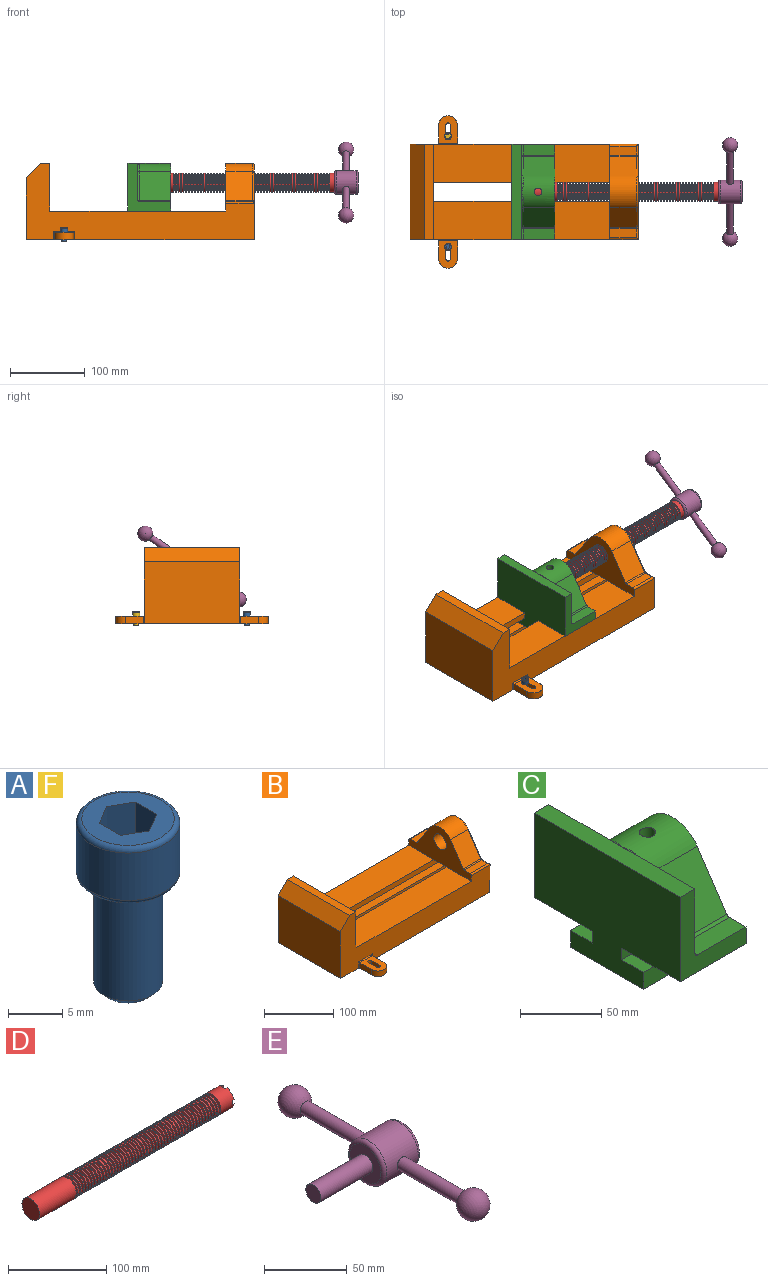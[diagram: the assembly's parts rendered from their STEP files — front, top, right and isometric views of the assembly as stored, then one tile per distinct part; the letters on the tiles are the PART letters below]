
ASSEMBLY  parts=6 mates=6
PART A: 15 faces, bbox 10.3x10.3x19.1 mm
  f0: plane 8.51x8.51mm, normal (0,0,1), area 37.2mm2, adj f5,f6,f7,f8,f9,f10,f14
  f1: cylinder r=3.17mm len=11.94mm, axis (0,0,1), area 238.2mm2, adj f4,f12
  f2: plane 4.83x4.83mm, normal (0,0,-1), area 18.3mm2, adj f12
  f3: cylinder r=4.76mm len=9.53mm, axis (0,0,-1), area 159.6mm2, adj f13,f14
  f4: plane 8.51x8.51mm, normal (0,0,-1), area 25.2mm2, adj f1,f13
  f5: plane 4.83x2.38mm, normal (-0.5,-0.87,0), area 13.3mm2, adj f0,f6,f10,f11
  f6: plane 4.83x2.38mm, normal (0.5,-0.87,0), area 13.3mm2, adj f0,f5,f7,f11
  f7: plane 4.83x2.75mm, normal (1,0,0), area 13.3mm2, adj f0,f6,f8,f11
  f8: plane 4.83x2.38mm, normal (0.5,0.87,0), area 13.3mm2, adj f0,f7,f9,f11
  f9: plane 4.83x2.38mm, normal (-0.5,0.87,0), area 13.3mm2, adj f0,f8,f10,f11
  f10: plane 4.83x2.75mm, normal (-1,0,0), area 13.3mm2, adj f0,f5,f9,f11
  f11: plane 5.5x4.76mm, normal (0,0,1), area 19.6mm2, adj f5,f6,f7,f8,f9,f10
  f12: cone r=3.17mm half-angle=45deg, axis (0,0,1), area 18.9mm2, adj f1,f2
  f13: torus R=4.25mm, axis (0,0,1), area 23mm2, adj f3,f4
  f14: torus R=4.25mm, axis (0,0,1), area 23mm2, adj f0,f3
PART B: 61 faces, bbox 304.8x203.2x103.7 mm
  f0: plane 304.8x101.6mm, normal (0,1,0), area 13520.3mm2, adj f3,f4,f5,f6,f7,f8,f9,f16
  f1: plane 304.8x101.6mm, normal (0,-1,0), area 13520.3mm2, adj f2,f3,f5,f6,f7,f8,f9,f16
  f2: plane 234.95x50.8mm, normal (0,0,1), area 11935.5mm2, adj f1,f5,f16,f26
  f3: plane 127x99.06mm, normal (1,0,0), area 7097.5mm2, adj f0,f1,f9,f14,f17,f18,f19,f20
  f4: plane 234.95x50.8mm, normal (0,0,1), area 11935.5mm2, adj f0,f5,f16,f27
  f5: plane 127x101.6mm, normal (1,0,0), area 9516.1mm2, adj f0,f1,f2,f4,f6,f9,f18,f19
  f6: plane 127x12.7mm, normal (0,0,1), area 1612.9mm2, adj f0,f1,f5,f7
  f7: plane 127x19.05mm, normal (-0.71,0,0.71), area 3421.5mm2, adj f0,f1,f6,f8
  f8: plane 127x82.55mm, normal (-1,0,0), area 10483.8mm2, adj f0,f1,f7,f9
  f9: plane 304.8x203.2mm, normal (0,0,-1), area 33298.3mm2, adj f0,f1,f3,f5,f8,f21,f22,f39
  f10: plane 35.56x11.98mm, normal (0,0,1), area 426mm2, adj f16,f28,f29,f30
  f11: plane 38.43x35.56mm, normal (0,0.83,0.56), area 1645.4mm2, adj f12,f16,f29,f32
  f12: cylinder r=25.4mm len=42.19mm, axis (1,0,0), area 1770.2mm2, adj f11,f13,f16,f33
  f13: plane 38.43x35.56mm, normal (0,-0.83,0.56), area 1645.4mm2, adj f12,f16,f34,f35
  f14: cylinder r=12.7mm len=38.1mm, axis (1,0,0), area 3040.2mm2, adj f3,f16
  f15: plane 35.56x11.98mm, normal (0,0,1), area 426mm2, adj f16,f34,f36,f38
  f16: plane 127x63.5mm, normal (-1,0,0), area 4155.5mm2, adj f0,f1,f2,f4,f10,f11,f12,f13
  f17: plane 38.1x25.4mm, normal (0,0,-1), area 967.7mm2, adj f3,f16,f26,f27
  f18: plane 273.05x19.05mm, normal (0,0,-1), area 5201.6mm2, adj f3,f5,f19,f26
  f19: plane 273.05x12.7mm, normal (0,1,0), area 3467.7mm2, adj f3,f5,f18,f20
  f20: plane 273.05x19.05mm, normal (0,0,1), area 5201.6mm2, adj f3,f5,f19,f21
  f21: plane 273.05x16.51mm, normal (0,1,0), area 4508.1mm2, adj f3,f5,f9,f20
  f22: plane 273.05x16.51mm, normal (0,-1,0), area 4508.1mm2, adj f3,f5,f9,f23
  f23: plane 273.05x19.05mm, normal (0,0,1), area 5201.6mm2, adj f3,f5,f22,f24
  f24: plane 273.05x12.7mm, normal (0,-1,0), area 3467.7mm2, adj f3,f5,f23,f25
  f25: plane 273.05x19.05mm, normal (0,0,-1), area 5201.6mm2, adj f3,f5,f24,f27
  f26: plane 273.05x8.89mm, normal (0,1,0), area 2427.4mm2, adj f2,f3,f5,f17,f18
  f27: plane 273.05x8.89mm, normal (0,-1,0), area 2427.4mm2, adj f3,f4,f5,f17,f25
  f28: cylinder r=2.54mm len=38.1mm, axis (1,0,0), area 148.3mm2, adj f0,f10,f16,f30
  f29: cylinder r=2.54mm len=35.56mm, axis (-1,0,0), area 88.5mm2, adj f10,f11,f16,f31
  f30: cylinder r=2.54mm len=14.52mm, axis (0,1,0), area 54.3mm2, adj f3,f10,f28,f31
  f31: torus R=5.08mm, axis (-1,0,0), area 13.5mm2, adj f3,f29,f30,f32
  f32: cylinder r=2.54mm len=39.84mm, axis (0,0.56,-0.83), area 184.6mm2, adj f3,f11,f31,f33
  f33: torus R=22.86mm, axis (-1,0,0), area 191.4mm2, adj f3,f12,f32,f35
  f34: cylinder r=2.54mm len=35.56mm, axis (-1,0,0), area 88.5mm2, adj f13,f15,f16,f37
  f35: cylinder r=2.54mm len=39.84mm, axis (0,0.56,0.83), area 184.6mm2, adj f3,f13,f33,f37
  f36: cylinder r=2.54mm len=38.1mm, axis (-1,0,0), area 148.3mm2, adj f1,f15,f16,f38
  f37: torus R=5.08mm, axis (-1,0,0), area 13.5mm2, adj f3,f34,f35,f38
  f38: cylinder r=2.54mm len=14.52mm, axis (0,1,0), area 54.3mm2, adj f3,f15,f36,f37
  f39: plane 23.88x9.53mm, normal (-1,0,0), area 227.4mm2, adj f9,f45,f46,f60
  f40: plane 23.88x9.53mm, normal (1,0,0), area 227.4mm2, adj f9,f45,f46,f58
  f41: cylinder r=3.3mm len=9.53mm, axis (0,0,-1), area 98.8mm2, adj f9,f42,f44,f46
  f42: plane 15.62x9.53mm, normal (-1,0,0), area 148.8mm2, adj f9,f41,f43,f46
  f43: cylinder r=3.3mm len=9.53mm, axis (0,0,-1), area 98.8mm2, adj f9,f42,f44,f46
  f44: plane 15.62x9.53mm, normal (1,0,0), area 148.8mm2, adj f9,f41,f43,f46
  f45: cylinder r=12.7mm len=25.4mm, axis (0,0,-1), area 380mm2, adj f9,f39,f40,f46
  f46: plane 36.58x25.4mm, normal (0,0,1), area 722.4mm2, adj f39,f40,f41,f42,f43,f44,f45,f59
  f47: plane 23.88x9.53mm, normal (-1,0,0), area 227.4mm2, adj f9,f53,f54,f56
  f48: plane 23.88x9.53mm, normal (1,0,0), area 227.4mm2, adj f9,f53,f54,f55
  f49: cylinder r=3.3mm len=9.53mm, axis (0,0,-1), area 98.8mm2, adj f9,f50,f52,f54
  f50: plane 15.62x9.53mm, normal (-1,0,0), area 148.8mm2, adj f9,f49,f51,f54
  f51: cylinder r=3.3mm len=9.53mm, axis (0,0,-1), area 98.8mm2, adj f9,f50,f52,f54
  f52: plane 15.62x9.53mm, normal (1,0,0), area 148.8mm2, adj f9,f49,f51,f54
  f53: cylinder r=12.7mm len=25.4mm, axis (0,0,-1), area 380mm2, adj f9,f47,f48,f54
  f54: plane 36.58x25.4mm, normal (0,0,1), area 722.4mm2, adj f47,f48,f49,f50,f51,f52,f53,f57
  f55: cylinder r=1.52mm len=11.05mm, axis (0,0,-1), area 24.1mm2, adj f0,f9,f48,f57
  f56: cylinder r=1.52mm len=11.05mm, axis (0,0,1), area 24.1mm2, adj f0,f9,f47,f57
  f57: cylinder r=1.52mm len=28.45mm, axis (1,0,0), area 63.5mm2, adj f0,f54,f55,f56
  f58: cylinder r=1.52mm len=11.05mm, axis (0,0,1), area 24.1mm2, adj f1,f9,f40,f59
  f59: cylinder r=1.52mm len=28.45mm, axis (-1,0,0), area 63.5mm2, adj f1,f46,f58,f60
  f60: cylinder r=1.52mm len=11.05mm, axis (0,0,-1), area 24.1mm2, adj f1,f9,f39,f59
PART C: 36 faces, bbox 57.2x127x89 mm
  f0: plane 57.15x50.8mm, normal (0,0,-1), area 2903.2mm2, adj f6,f9,f10,f23
  f1: cylinder r=12.7mm len=44.45mm, axis (1,0,0), area 3464.3mm2, adj f6,f15,f16
  f2: plane 41.91x14.52mm, normal (0,0,1), area 608.5mm2, adj f6,f11,f24,f25
  f3: plane 51.86x48.26mm, normal (1,0,0), area 1495.7mm2, adj f8,f10,f31,f33,f35
  f4: plane 51.86x48.26mm, normal (1,0,0), area 1495.7mm2, adj f8,f11,f24,f28,f29
  f5: plane 57.15x50.8mm, normal (0,0,-1), area 2903.2mm2, adj f6,f9,f11,f22
  f6: plane 127x85.09mm, normal (1,0,0), area 5190.6mm2, adj f0,f1,f2,f5,f7,f10,f11,f12
  f7: plane 41.91x14.52mm, normal (0,0,1), area 608.5mm2, adj f6,f10,f30,f31
  f8: plane 127x12.7mm, normal (0,0,1), area 1612.9mm2, adj f3,f4,f9,f10,f11,f26,f34
  f9: plane 127x85.09mm, normal (-1,0,0), area 9096.8mm2, adj f0,f5,f8,f10,f11,f17,f18,f19
  f10: plane 63.5x57.15mm, normal (0,-1,0), area 1372.3mm2, adj f0,f3,f6,f7,f8,f9,f31
  f11: plane 63.5x57.15mm, normal (0,1,0), area 1372.3mm2, adj f2,f4,f5,f6,f8,f9,f24
  f12: plane 41.91x38.43mm, normal (0,-0.83,0.56), area 1939.2mm2, adj f6,f13,f30,f33
  f13: cylinder r=25.4mm len=44.45mm, axis (1,0,0), area 2026.5mm2, adj f6,f12,f14,f16,f26,f28,f34,f35
  f14: plane 41.91x38.43mm, normal (0,0.83,0.56), area 1939.2mm2, adj f6,f13,f25,f29
  f15: plane 25.4x25.4mm, normal (1,0,0), area 506.7mm2, adj f1
  f16: cylinder r=5.08mm len=13.76mm, axis (0,0,1), area 414mm2, adj f1,f13
  f17: plane 57.15x19.05mm, normal (0,0,1), area 1088.7mm2, adj f6,f9,f18,f23
  f18: plane 57.15x12.7mm, normal (0,-1,0), area 725.8mm2, adj f6,f9,f17,f19
  f19: plane 63.5x57.15mm, normal (0,0,-1), area 3629mm2, adj f6,f9,f18,f20
  f20: plane 57.15x12.7mm, normal (0,1,0), area 725.8mm2, adj f6,f9,f19,f21
  f21: plane 57.15x19.05mm, normal (0,0,1), area 1088.7mm2, adj f6,f9,f20,f22
  f22: plane 57.15x8.89mm, normal (0,1,0), area 508.1mm2, adj f5,f6,f9,f21
  f23: plane 57.15x8.89mm, normal (0,-1,0), area 508.1mm2, adj f0,f6,f9,f17
  f24: cylinder r=2.54mm len=14.52mm, axis (0,-1,0), area 57.9mm2, adj f2,f4,f11,f27
  f25: cylinder r=2.54mm len=41.91mm, axis (1,0,0), area 104.3mm2, adj f2,f6,f14,f27
  f26: bspline ~12.24x2.8mm, area 20.9mm2, adj f8,f13,f28
  f27: sphere r=2.54mm, area 6.3mm2, adj f24,f25,f29
  f28: torus R=27.94mm, axis (1,0,0), area 57.8mm2, adj f4,f13,f26,f29
  f29: cylinder r=2.54mm len=39.84mm, axis (0,-0.56,0.83), area 184.6mm2, adj f4,f14,f27,f28
  f30: cylinder r=2.54mm len=41.91mm, axis (1,0,0), area 104.3mm2, adj f6,f7,f12,f32
  f31: cylinder r=2.54mm len=14.52mm, axis (0,-1,0), area 57.9mm2, adj f3,f7,f10,f32
  f32: sphere r=2.54mm, area 6.3mm2, adj f30,f31,f33
  f33: cylinder r=2.54mm len=39.84mm, axis (0,-0.56,-0.83), area 184.6mm2, adj f3,f12,f32,f35
  f34: bspline ~12.24x2.8mm, area 20.9mm2, adj f8,f13,f35
  f35: torus R=27.94mm, axis (1,0,0), area 57.8mm2, adj f3,f13,f33,f34
PART D: 220 faces, bbox 279.4x25.4x25.4 mm
  f0: cylinder r=12.7mm len=25.4mm, axis (-1,0,0), area 1468.2mm2, adj f1,f2,f3,f5,f7,f208,f209,f210
  f1: plane 9.9x9.9mm, normal (1,0,0), area 62.3mm2, adj f0,f4,f213,f216
  f2: plane 9.9x9.9mm, normal (1,0,0), area 62.3mm2, adj f0,f4,f210,f218
  f3: plane 9.9x9.9mm, normal (1,0,0), area 62.3mm2, adj f0,f4,f209,f212
  f4: cylinder r=6.35mm len=25.4mm, axis (1,0,0), area 960.3mm2, adj f1,f2,f3,f5,f6,f208,f209,f210
  f5: plane 9.9x9.9mm, normal (1,0,0), area 62.3mm2, adj f0,f4,f215,f217
  f6: plane 12.7x12.7mm, normal (1,0,0), area 126.7mm2, adj f4
  f7: cone r=12.7mm half-angle=76deg, axis (1,0,0), area 188mm2, adj f0,f9
  f8: cone r=10.16mm half-angle=76deg, axis (-1,0,0), area 188mm2, adj f9,f10
  f9: cylinder r=10.16mm len=20.32mm, axis (1,0,0), area 81.1mm2, adj f7,f8
  f10: cylinder r=12.7mm len=25.4mm, axis (-1,0,0), area 131.7mm2, adj f8,f11
  f11: cone r=12.7mm half-angle=76deg, axis (1,0,0), area 188mm2, adj f10,f13
  f12: cone r=10.16mm half-angle=76deg, axis (-1,0,0), area 188mm2, adj f13,f14
  f13: cylinder r=10.16mm len=20.32mm, axis (1,0,0), area 81.1mm2, adj f11,f12
  f14: cylinder r=12.7mm len=25.4mm, axis (-1,0,0), area 131.7mm2, adj f12,f15
  f15: cone r=12.7mm half-angle=76deg, axis (1,0,0), area 188mm2, adj f14,f17
  f16: cone r=10.16mm half-angle=76deg, axis (-1,0,0), area 188mm2, adj f17,f18
  f17: cylinder r=10.16mm len=20.32mm, axis (1,0,0), area 81.1mm2, adj f15,f16
  f18: cylinder r=12.7mm len=25.4mm, axis (-1,0,0), area 131.7mm2, adj f16,f19
  f19: cone r=12.7mm half-angle=76deg, axis (1,0,0), area 188mm2, adj f18,f21
  f20: cone r=10.16mm half-angle=76deg, axis (-1,0,0), area 188mm2, adj f21,f22
  f21: cylinder r=10.16mm len=20.32mm, axis (1,0,0), area 81.1mm2, adj f19,f20
  f22: cylinder r=12.7mm len=25.4mm, axis (-1,0,0), area 131.7mm2, adj f20,f23
  f23: cone r=12.7mm half-angle=76deg, axis (1,0,0), area 188mm2, adj f22,f25
  f24: cone r=10.16mm half-angle=76deg, axis (-1,0,0), area 188mm2, adj f25,f26
  f25: cylinder r=10.16mm len=20.32mm, axis (1,0,0), area 81.1mm2, adj f23,f24
  f26: cylinder r=12.7mm len=25.4mm, axis (-1,0,0), area 131.7mm2, adj f24,f27
  f27: cone r=12.7mm half-angle=76deg, axis (1,0,0), area 188mm2, adj f26,f29
  f28: cone r=10.16mm half-angle=76deg, axis (-1,0,0), area 188mm2, adj f29,f30
  f29: cylinder r=10.16mm len=20.32mm, axis (1,0,0), area 81.1mm2, adj f27,f28
  f30: cylinder r=12.7mm len=25.4mm, axis (-1,0,0), area 131.7mm2, adj f28,f31
  f31: cone r=12.7mm half-angle=76deg, axis (1,0,0), area 188mm2, adj f30,f33
  f32: cone r=10.16mm half-angle=76deg, axis (-1,0,0), area 188mm2, adj f33,f34
  f33: cylinder r=10.16mm len=20.32mm, axis (1,0,0), area 81.1mm2, adj f31,f32
  f34: cylinder r=12.7mm len=25.4mm, axis (-1,0,0), area 131.7mm2, adj f32,f35
  f35: cone r=12.7mm half-angle=76deg, axis (1,0,0), area 188mm2, adj f34,f37
  f36: cone r=10.16mm half-angle=76deg, axis (-1,0,0), area 188mm2, adj f37,f38
  f37: cylinder r=10.16mm len=20.32mm, axis (1,0,0), area 81.1mm2, adj f35,f36
  f38: cylinder r=12.7mm len=25.4mm, axis (-1,0,0), area 131.7mm2, adj f36,f39
  f39: cone r=12.7mm half-angle=76deg, axis (1,0,0), area 188mm2, adj f38,f41
  f40: cone r=10.16mm half-angle=76deg, axis (-1,0,0), area 188mm2, adj f41,f42
  f41: cylinder r=10.16mm len=20.32mm, axis (1,0,0), area 81.1mm2, adj f39,f40
  f42: cylinder r=12.7mm len=25.4mm, axis (-1,0,0), area 131.7mm2, adj f40,f43
  f43: cone r=12.7mm half-angle=76deg, axis (1,0,0), area 188mm2, adj f42,f45
  f44: cone r=10.16mm half-angle=76deg, axis (-1,0,0), area 188mm2, adj f45,f46
  f45: cylinder r=10.16mm len=20.32mm, axis (1,0,0), area 81.1mm2, adj f43,f44
  f46: cylinder r=12.7mm len=25.4mm, axis (-1,0,0), area 131.7mm2, adj f44,f47
  f47: cone r=12.7mm half-angle=76deg, axis (1,0,0), area 188mm2, adj f46,f49
  f48: cone r=10.16mm half-angle=76deg, axis (-1,0,0), area 188mm2, adj f49,f50
  f49: cylinder r=10.16mm len=20.32mm, axis (1,0,0), area 81.1mm2, adj f47,f48
  f50: cylinder r=12.7mm len=25.4mm, axis (-1,0,0), area 131.7mm2, adj f48,f51
  f51: cone r=12.7mm half-angle=76deg, axis (1,0,0), area 188mm2, adj f50,f53
  f52: cone r=10.16mm half-angle=76deg, axis (-1,0,0), area 188mm2, adj f53,f54
  f53: cylinder r=10.16mm len=20.32mm, axis (1,0,0), area 81.1mm2, adj f51,f52
  f54: cylinder r=12.7mm len=25.4mm, axis (-1,0,0), area 131.7mm2, adj f52,f55
  f55: cone r=12.7mm half-angle=76deg, axis (1,0,0), area 188mm2, adj f54,f57
  f56: cone r=10.16mm half-angle=76deg, axis (-1,0,0), area 188mm2, adj f57,f58
  f57: cylinder r=10.16mm len=20.32mm, axis (1,0,0), area 81.1mm2, adj f55,f56
  f58: cylinder r=12.7mm len=25.4mm, axis (-1,0,0), area 131.7mm2, adj f56,f59
  f59: cone r=12.7mm half-angle=76deg, axis (1,0,0), area 188mm2, adj f58,f61
  f60: cone r=10.16mm half-angle=76deg, axis (-1,0,0), area 188mm2, adj f61,f62
  f61: cylinder r=10.16mm len=20.32mm, axis (1,0,0), area 81.1mm2, adj f59,f60
  f62: cylinder r=12.7mm len=25.4mm, axis (-1,0,0), area 131.7mm2, adj f60,f63
  f63: cone r=12.7mm half-angle=76deg, axis (1,0,0), area 188mm2, adj f62,f65
  f64: cone r=10.16mm half-angle=76deg, axis (-1,0,0), area 188mm2, adj f65,f66
  f65: cylinder r=10.16mm len=20.32mm, axis (1,0,0), area 81.1mm2, adj f63,f64
  f66: cylinder r=12.7mm len=25.4mm, axis (-1,0,0), area 131.7mm2, adj f64,f67
  f67: cone r=12.7mm half-angle=76deg, axis (1,0,0), area 188mm2, adj f66,f69
  f68: cone r=10.16mm half-angle=76deg, axis (-1,0,0), area 188mm2, adj f69,f70
  f69: cylinder r=10.16mm len=20.32mm, axis (1,0,0), area 81.1mm2, adj f67,f68
  f70: cylinder r=12.7mm len=25.4mm, axis (-1,0,0), area 131.7mm2, adj f68,f71
  f71: cone r=12.7mm half-angle=76deg, axis (1,0,0), area 188mm2, adj f70,f73
  f72: cone r=10.16mm half-angle=76deg, axis (-1,0,0), area 188mm2, adj f73,f74
  f73: cylinder r=10.16mm len=20.32mm, axis (1,0,0), area 81.1mm2, adj f71,f72
  f74: cylinder r=12.7mm len=25.4mm, axis (-1,0,0), area 131.7mm2, adj f72,f75
  f75: cone r=12.7mm half-angle=76deg, axis (1,0,0), area 188mm2, adj f74,f77
  f76: cone r=10.16mm half-angle=76deg, axis (-1,0,0), area 188mm2, adj f77,f78
  f77: cylinder r=10.16mm len=20.32mm, axis (1,0,0), area 81.1mm2, adj f75,f76
  f78: cylinder r=12.7mm len=25.4mm, axis (-1,0,0), area 131.7mm2, adj f76,f79
  f79: cone r=12.7mm half-angle=76deg, axis (1,0,0), area 188mm2, adj f78,f81
  f80: cone r=10.16mm half-angle=76deg, axis (-1,0,0), area 188mm2, adj f81,f82
  f81: cylinder r=10.16mm len=20.32mm, axis (1,0,0), area 81.1mm2, adj f79,f80
  f82: cylinder r=12.7mm len=25.4mm, axis (-1,0,0), area 131.7mm2, adj f80,f83
  f83: cone r=12.7mm half-angle=76deg, axis (1,0,0), area 188mm2, adj f82,f85
  f84: cone r=10.16mm half-angle=76deg, axis (-1,0,0), area 188mm2, adj f85,f86
  f85: cylinder r=10.16mm len=20.32mm, axis (1,0,0), area 81.1mm2, adj f83,f84
  f86: cylinder r=12.7mm len=25.4mm, axis (-1,0,0), area 131.7mm2, adj f84,f87
  f87: cone r=12.7mm half-angle=76deg, axis (1,0,0), area 188mm2, adj f86,f89
  f88: cone r=10.16mm half-angle=76deg, axis (-1,0,0), area 188mm2, adj f89,f90
  f89: cylinder r=10.16mm len=20.32mm, axis (1,0,0), area 81.1mm2, adj f87,f88
  f90: cylinder r=12.7mm len=25.4mm, axis (-1,0,0), area 131.7mm2, adj f88,f91
  f91: cone r=12.7mm half-angle=76deg, axis (1,0,0), area 188mm2, adj f90,f93
  f92: cone r=10.16mm half-angle=76deg, axis (-1,0,0), area 188mm2, adj f93,f94
  f93: cylinder r=10.16mm len=20.32mm, axis (1,0,0), area 81.1mm2, adj f91,f92
  f94: cylinder r=12.7mm len=25.4mm, axis (-1,0,0), area 131.7mm2, adj f92,f95
  f95: cone r=12.7mm half-angle=76deg, axis (1,0,0), area 188mm2, adj f94,f97
  f96: cone r=10.16mm half-angle=76deg, axis (-1,0,0), area 188mm2, adj f97,f98
  f97: cylinder r=10.16mm len=20.32mm, axis (1,0,0), area 81.1mm2, adj f95,f96
  f98: cylinder r=12.7mm len=25.4mm, axis (-1,0,0), area 131.7mm2, adj f96,f99
  f99: cone r=12.7mm half-angle=76deg, axis (1,0,0), area 188mm2, adj f98,f101
  f100: cone r=10.16mm half-angle=76deg, axis (-1,0,0), area 188mm2, adj f101,f102
  f101: cylinder r=10.16mm len=20.32mm, axis (1,0,0), area 81.1mm2, adj f99,f100
  f102: cylinder r=12.7mm len=25.4mm, axis (-1,0,0), area 131.7mm2, adj f100,f103
  f103: cone r=12.7mm half-angle=76deg, axis (1,0,0), area 188mm2, adj f102,f105
  f104: cone r=10.16mm half-angle=76deg, axis (-1,0,0), area 188mm2, adj f105,f106
  f105: cylinder r=10.16mm len=20.32mm, axis (1,0,0), area 81.1mm2, adj f103,f104
  f106: cylinder r=12.7mm len=25.4mm, axis (-1,0,0), area 131.7mm2, adj f104,f107
  f107: cone r=12.7mm half-angle=76deg, axis (1,0,0), area 188mm2, adj f106,f109
  f108: cone r=10.16mm half-angle=76deg, axis (-1,0,0), area 188mm2, adj f109,f110
  f109: cylinder r=10.16mm len=20.32mm, axis (1,0,0), area 81.1mm2, adj f107,f108
  f110: cylinder r=12.7mm len=25.4mm, axis (-1,0,0), area 131.7mm2, adj f108,f111
  f111: cone r=12.7mm half-angle=76deg, axis (1,0,0), area 188mm2, adj f110,f113
  f112: cone r=10.16mm half-angle=76deg, axis (-1,0,0), area 188mm2, adj f113,f114
  f113: cylinder r=10.16mm len=20.32mm, axis (1,0,0), area 81.1mm2, adj f111,f112
  f114: cylinder r=12.7mm len=25.4mm, axis (-1,0,0), area 131.7mm2, adj f112,f115
  f115: cone r=12.7mm half-angle=76deg, axis (1,0,0), area 188mm2, adj f114,f117
  f116: cone r=10.16mm half-angle=76deg, axis (-1,0,0), area 188mm2, adj f117,f118
  f117: cylinder r=10.16mm len=20.32mm, axis (1,0,0), area 81.1mm2, adj f115,f116
  f118: cylinder r=12.7mm len=25.4mm, axis (-1,0,0), area 131.7mm2, adj f116,f119
  f119: cone r=12.7mm half-angle=76deg, axis (1,0,0), area 188mm2, adj f118,f121
  f120: cone r=10.16mm half-angle=76deg, axis (-1,0,0), area 188mm2, adj f121,f122
  f121: cylinder r=10.16mm len=20.32mm, axis (1,0,0), area 81.1mm2, adj f119,f120
  f122: cylinder r=12.7mm len=25.4mm, axis (-1,0,0), area 131.7mm2, adj f120,f123
  f123: cone r=12.7mm half-angle=76deg, axis (1,0,0), area 188mm2, adj f122,f125
  f124: cone r=10.16mm half-angle=76deg, axis (-1,0,0), area 188mm2, adj f125,f126
  f125: cylinder r=10.16mm len=20.32mm, axis (1,0,0), area 81.1mm2, adj f123,f124
  f126: cylinder r=12.7mm len=25.4mm, axis (-1,0,0), area 131.7mm2, adj f124,f127
  f127: cone r=12.7mm half-angle=76deg, axis (1,0,0), area 188mm2, adj f126,f129
  f128: cone r=10.16mm half-angle=76deg, axis (-1,0,0), area 188mm2, adj f129,f130
  f129: cylinder r=10.16mm len=20.32mm, axis (1,0,0), area 81.1mm2, adj f127,f128
  f130: cylinder r=12.7mm len=25.4mm, axis (-1,0,0), area 131.7mm2, adj f128,f131
  f131: cone r=12.7mm half-angle=76deg, axis (1,0,0), area 188mm2, adj f130,f133
  f132: cone r=10.16mm half-angle=76deg, axis (-1,0,0), area 188mm2, adj f133,f134
  f133: cylinder r=10.16mm len=20.32mm, axis (1,0,0), area 81.1mm2, adj f131,f132
  f134: cylinder r=12.7mm len=25.4mm, axis (-1,0,0), area 131.7mm2, adj f132,f135
  f135: cone r=12.7mm half-angle=76deg, axis (1,0,0), area 188mm2, adj f134,f137
  f136: cone r=10.16mm half-angle=76deg, axis (-1,0,0), area 188mm2, adj f137,f138
  f137: cylinder r=10.16mm len=20.32mm, axis (1,0,0), area 81.1mm2, adj f135,f136
  f138: cylinder r=12.7mm len=25.4mm, axis (-1,0,0), area 131.7mm2, adj f136,f139
  f139: cone r=12.7mm half-angle=76deg, axis (1,0,0), area 188mm2, adj f138,f141
  f140: cone r=10.16mm half-angle=76deg, axis (-1,0,0), area 188mm2, adj f141,f142
  f141: cylinder r=10.16mm len=20.32mm, axis (1,0,0), area 81.1mm2, adj f139,f140
  f142: cylinder r=12.7mm len=25.4mm, axis (-1,0,0), area 131.7mm2, adj f140,f143
  f143: cone r=12.7mm half-angle=76deg, axis (1,0,0), area 188mm2, adj f142,f145
  f144: cone r=10.16mm half-angle=76deg, axis (-1,0,0), area 188mm2, adj f145,f146
  f145: cylinder r=10.16mm len=20.32mm, axis (1,0,0), area 81.1mm2, adj f143,f144
  f146: cylinder r=12.7mm len=25.4mm, axis (-1,0,0), area 131.7mm2, adj f144,f147
  f147: cone r=12.7mm half-angle=76deg, axis (1,0,0), area 188mm2, adj f146,f149
  f148: cone r=10.16mm half-angle=76deg, axis (-1,0,0), area 188mm2, adj f149,f150
  f149: cylinder r=10.16mm len=20.32mm, axis (1,0,0), area 81.1mm2, adj f147,f148
  f150: cylinder r=12.7mm len=25.4mm, axis (-1,0,0), area 131.7mm2, adj f148,f151
  f151: cone r=12.7mm half-angle=76deg, axis (1,0,0), area 188mm2, adj f150,f153
  f152: cone r=10.16mm half-angle=76deg, axis (-1,0,0), area 188mm2, adj f153,f154
  f153: cylinder r=10.16mm len=20.32mm, axis (1,0,0), area 81.1mm2, adj f151,f152
  f154: cylinder r=12.7mm len=25.4mm, axis (-1,0,0), area 131.7mm2, adj f152,f155
  f155: cone r=12.7mm half-angle=76deg, axis (1,0,0), area 188mm2, adj f154,f157
  f156: cone r=10.16mm half-angle=76deg, axis (-1,0,0), area 188mm2, adj f157,f158
  f157: cylinder r=10.16mm len=20.32mm, axis (1,0,0), area 81.1mm2, adj f155,f156
  f158: cylinder r=12.7mm len=25.4mm, axis (-1,0,0), area 131.7mm2, adj f156,f159
  f159: cone r=12.7mm half-angle=76deg, axis (1,0,0), area 188mm2, adj f158,f161
  f160: cone r=10.16mm half-angle=76deg, axis (-1,0,0), area 188mm2, adj f161,f162
  f161: cylinder r=10.16mm len=20.32mm, axis (1,0,0), area 81.1mm2, adj f159,f160
  f162: cylinder r=12.7mm len=25.4mm, axis (-1,0,0), area 131.7mm2, adj f160,f163
  f163: cone r=12.7mm half-angle=76deg, axis (1,0,0), area 188mm2, adj f162,f165
  f164: cone r=10.16mm half-angle=76deg, axis (-1,0,0), area 188mm2, adj f165,f166
  f165: cylinder r=10.16mm len=20.32mm, axis (1,0,0), area 81.1mm2, adj f163,f164
  f166: cylinder r=12.7mm len=25.4mm, axis (-1,0,0), area 131.7mm2, adj f164,f167
  f167: cone r=12.7mm half-angle=76deg, axis (1,0,0), area 188mm2, adj f166,f169
  f168: cone r=10.16mm half-angle=76deg, axis (-1,0,0), area 188mm2, adj f169,f170
  f169: cylinder r=10.16mm len=20.32mm, axis (1,0,0), area 81.1mm2, adj f167,f168
  f170: cylinder r=12.7mm len=25.4mm, axis (-1,0,0), area 131.7mm2, adj f168,f171
  f171: cone r=12.7mm half-angle=76deg, axis (1,0,0), area 188mm2, adj f170,f173
  f172: cone r=10.16mm half-angle=76deg, axis (-1,0,0), area 188mm2, adj f173,f174
  f173: cylinder r=10.16mm len=20.32mm, axis (1,0,0), area 81.1mm2, adj f171,f172
  f174: cylinder r=12.7mm len=25.4mm, axis (-1,0,0), area 131.7mm2, adj f172,f175
  f175: cone r=12.7mm half-angle=76deg, axis (1,0,0), area 188mm2, adj f174,f177
  f176: cone r=10.16mm half-angle=76deg, axis (-1,0,0), area 188mm2, adj f177,f178
  f177: cylinder r=10.16mm len=20.32mm, axis (1,0,0), area 81.1mm2, adj f175,f176
  f178: cylinder r=12.7mm len=25.4mm, axis (-1,0,0), area 131.7mm2, adj f176,f179
  f179: cone r=12.7mm half-angle=76deg, axis (1,0,0), area 188mm2, adj f178,f181
  f180: cone r=10.16mm half-angle=76deg, axis (-1,0,0), area 188mm2, adj f181,f182
  f181: cylinder r=10.16mm len=20.32mm, axis (1,0,0), area 81.1mm2, adj f179,f180
  f182: cylinder r=12.7mm len=25.4mm, axis (-1,0,0), area 131.7mm2, adj f180,f183
  f183: cone r=12.7mm half-angle=76deg, axis (1,0,0), area 188mm2, adj f182,f185
  f184: cone r=10.16mm half-angle=76deg, axis (-1,0,0), area 188mm2, adj f185,f186
  f185: cylinder r=10.16mm len=20.32mm, axis (1,0,0), area 81.1mm2, adj f183,f184
  f186: cylinder r=12.7mm len=25.4mm, axis (-1,0,0), area 131.7mm2, adj f184,f187
  f187: cone r=12.7mm half-angle=76deg, axis (1,0,0), area 188mm2, adj f186,f189
  f188: cone r=10.16mm half-angle=76deg, axis (-1,0,0), area 188mm2, adj f189,f190
  f189: cylinder r=10.16mm len=20.32mm, axis (1,0,0), area 81.1mm2, adj f187,f188
  f190: cylinder r=12.7mm len=25.4mm, axis (-1,0,0), area 131.7mm2, adj f188,f191
  f191: cone r=12.7mm half-angle=76deg, axis (1,0,0), area 188mm2, adj f190,f193
  f192: cone r=10.16mm half-angle=76deg, axis (-1,0,0), area 188mm2, adj f193,f194
  f193: cylinder r=10.16mm len=20.32mm, axis (1,0,0), area 81.1mm2, adj f191,f192
  f194: cylinder r=12.7mm len=25.4mm, axis (-1,0,0), area 131.7mm2, adj f192,f195
  f195: cone r=12.7mm half-angle=76deg, axis (1,0,0), area 188mm2, adj f194,f197
  f196: cone r=10.16mm half-angle=76deg, axis (-1,0,0), area 188mm2, adj f197,f198
  f197: cylinder r=10.16mm len=20.32mm, axis (1,0,0), area 81.1mm2, adj f195,f196
  f198: cylinder r=12.7mm len=25.4mm, axis (-1,0,0), area 131.7mm2, adj f196,f199
  f199: cone r=12.7mm half-angle=76deg, axis (1,0,0), area 188mm2, adj f198,f201
  f200: cone r=10.16mm half-angle=76deg, axis (-1,0,0), area 188mm2, adj f201,f202
  f201: cylinder r=10.16mm len=20.32mm, axis (1,0,0), area 81.1mm2, adj f199,f200
  f202: cylinder r=12.7mm len=25.4mm, axis (-1,0,0), area 131.7mm2, adj f200,f203
  f203: cone r=12.7mm half-angle=76deg, axis (1,0,0), area 188mm2, adj f202,f205
  f204: cone r=10.16mm half-angle=76deg, axis (-1,0,0), area 188mm2, adj f205,f207
  f205: cylinder r=10.16mm len=20.32mm, axis (1,0,0), area 81.1mm2, adj f203,f204
  f206: plane 25.4x25.4mm, normal (-1,0,0), area 506.7mm2, adj f207
  f207: cylinder r=12.7mm len=52.45mm, axis (-1,0,0), area 4185.4mm2, adj f204,f206
  f208: plane 6.88x5.08mm, normal (1,0,0), area 32.7mm2, adj f0,f4,f209,f210
  f209: plane 6.62x2.54mm, normal (0,-1,0), area 16.8mm2, adj f0,f3,f4,f208
  f210: plane 6.62x2.54mm, normal (0,1,0), area 16.8mm2, adj f0,f2,f4,f208
  f211: plane 6.88x5.08mm, normal (1,0,0), area 32.7mm2, adj f0,f4,f212,f213
  f212: plane 6.62x2.54mm, normal (0,0,1), area 16.8mm2, adj f0,f3,f4,f211
  f213: plane 6.62x2.54mm, normal (0,0,-1), area 16.8mm2, adj f0,f1,f4,f211
  f214: plane 6.88x5.08mm, normal (1,0,0), area 32.7mm2, adj f0,f4,f215,f216
  f215: plane 6.62x2.54mm, normal (0,1,0), area 16.8mm2, adj f0,f4,f5,f214
  f216: plane 6.62x2.54mm, normal (0,-1,0), area 16.8mm2, adj f0,f1,f4,f214
  f217: plane 6.62x2.54mm, normal (0,0,-1), area 16.8mm2, adj f0,f4,f5,f219
  f218: plane 6.62x2.54mm, normal (0,0,1), area 16.8mm2, adj f0,f2,f4,f219
  f219: plane 6.88x5.08mm, normal (1,0,0), area 32.7mm2, adj f0,f4,f217,f218
PART E: 11 faces, bbox 76.2x172.7x34.4 mm
  f0: sphere r=10.16mm, area 1231.8mm2, adj f1
  f1: cylinder r=4.45mm len=51.82mm, axis (0,1,0), area 1438.5mm2, adj f0,f4
  f2: sphere r=10.16mm, area 1231.8mm2, adj f3
  f3: cylinder r=4.45mm len=51.82mm, axis (0,1,0), area 1438.5mm2, adj f2,f4
  f4: cylinder r=15.88mm len=31.75mm, axis (-1,0,0), area 2534.7mm2, adj f1,f3,f9,f10
  f5: cylinder r=6.35mm len=44.45mm, axis (-1,0,0), area 1773.5mm2, adj f6,f8
  f6: plane 12.7x12.7mm, normal (-1,0,0), area 126.7mm2, adj f5
  f7: plane 26.67x26.67mm, normal (1,0,0), area 558.6mm2, adj f10
  f8: plane 26.67x26.67mm, normal (-1,0,0), area 432mm2, adj f5,f9
  f9: torus R=13.33mm, axis (1,0,0), area 374.8mm2, adj f4,f8
  f10: torus R=13.33mm, axis (1,0,0), area 374.8mm2, adj f4,f7
PART F: same geometry as A
PLACE A rot(axis=(0,0,-1),49.8deg) t=(-254,-73.28,9.53)mm
PLACE B at identity fixed
PLACE C t=(104.36,0,0)mm
PLACE D rot(axis=(-1,0,0),144.8deg) t=(100.36,-43.91,138.48)mm
PLACE E rot(axis=(-1,0,0),144.8deg) t=(68.61,-43.91,138.48)mm
PLACE F rot(axis=(0,0,-1),27.4deg) t=(-254,74.4,9.53)mm
MATE slider B.f5 <-> C.f9  axis (1,0,0) through (-273.05,0,101.6)mm
MATE pin_slot A.f1 <-> B.f43  axis (0,0,1) through (-254,-73.28,9.52)mm
MATE fastened E.f5 <-> D.f4  axis (-1,0,0) through (106.71,0,76.2)mm
MATE pin_slot F.f1 <-> B.f51  axis (0,0,1) through (-254,74.4,9.52)mm
MATE revolute D.f7 <-> C.f28  axis (-1,0,0) through (-133.77,0,76.2)mm
MATE cylindrical D.f7 <-> B.f12  axis (-1,0,0) through (-159.99,0,76.2)mm
